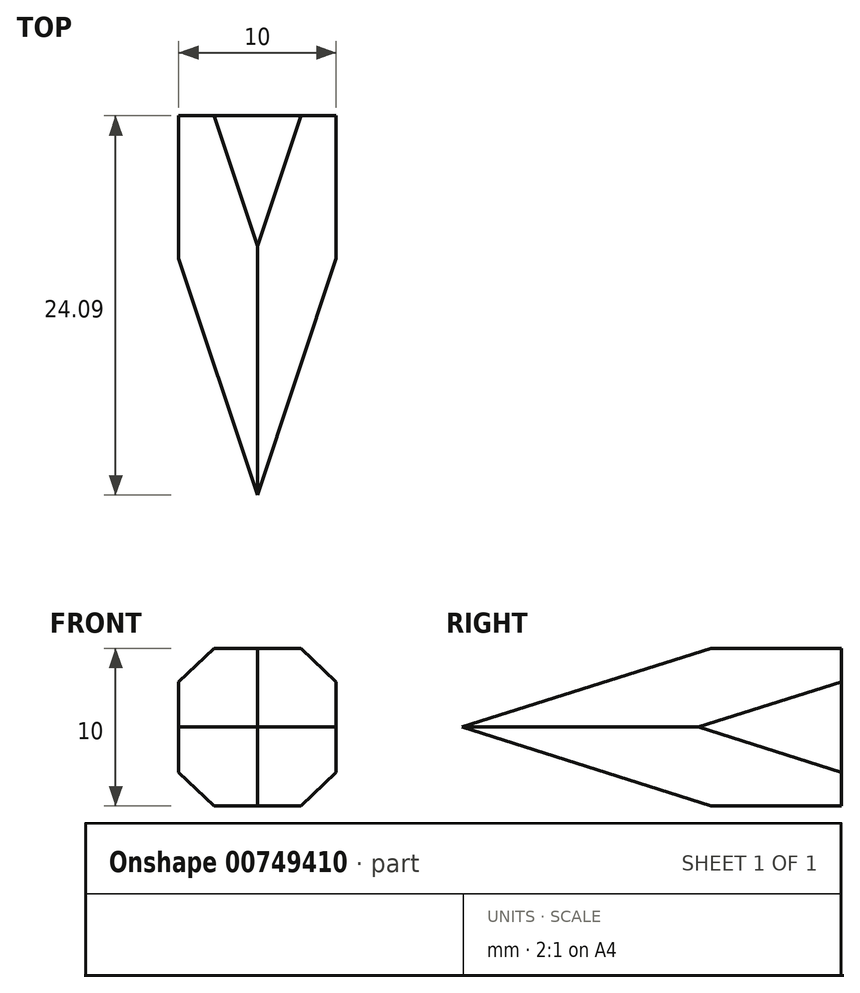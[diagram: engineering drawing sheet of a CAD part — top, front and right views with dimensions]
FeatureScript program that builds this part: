
annotation { "Feature Type Name" : "Feature", "Feature Type Description" : "" }
export const myFeature = defineFeature(function(context is Context, id is Id, definition is map)
    precondition{}
    {
        {
            var Q0;
            Q0=qCreatedBy(makeId("Top.planeOp"),FACE);
            var sketch = newSketch(context, id + "F0", { "sketchPlane" : qUnion([Q0])});
            skPoint(sketch, "E0.middle", {"position": v(0, 0) * mm});
            skLineSegment(sketch, "E1", {"start": v(0, -7.5) * mm, "end": v(-5, 7.5) * mm});
            skLineSegment(sketch, "E2", {"start": v(0, -7.5) * mm, "end": v(5, 7.5) * mm});
            skPoint(sketch, "E3.orphan", {"position": v(5, -7.5) * mm});
            skPoint(sketch, "E0.right.end.orphan", {"position": v(-5, -7.5) * mm});
            skLineSegment(sketch, "E4.bottom", {"start": v(-5, 16.59) * mm, "end": v(5, 16.59) * mm});
            skLineSegment(sketch, "E4.left", {"start": v(-5, 16.59) * mm, "end": v(-5, 7.5) * mm});
            skLineSegment(sketch, "E4.right", {"start": v(5, 16.59) * mm, "end": v(5, 7.5) * mm});
            skPoint(sketch, "E4.middle", {"position": v(0, 7.5) * mm});
            skPoint(sketch, "E5.orphan", {"position": v(-5, -1.59) * mm});
            skPoint(sketch, "E6.orphan", {"position": v(5, -1.59) * mm});
            skSolve(sketch);
        }
        {
            var Q0;
            Q0 = qSketchRegion(id + "F0", true);
            extrude(context, id + "F1", {"entities" : qUnion([Q0]), "endBound" : BoundingType.SYMMETRIC, "depth" : 10 * mm, "offsetDistance" : 25 * mm});
        }
        {
            var Q0;
            Q0=makeQuery(id+"F1.opExtrude","CAP_EDGE",EDGE,{"disambiguationData":[OSD([sQuery(id+"F0.wireOp",EDGE,"E2")])],"isStart":true});
            var Q1;
            Q1=makeQuery(id+"F1.opExtrude","CAP_EDGE",EDGE,{"disambiguationData":[OSD([sQuery(id+"F0.wireOp",EDGE,"E1")])],"isStart":true});
            var Q2;
            Q2=makeQuery(id+"F1.opExtrude","CAP_EDGE",EDGE,{"disambiguationData":[OSD([sQuery(id+"F0.wireOp",EDGE,"E2")])],"isStart":false});
            var Q3;
            Q3=makeQuery(id+"F1.opExtrude","CAP_EDGE",EDGE,{"disambiguationData":[OSD([sQuery(id+"F0.wireOp",EDGE,"E1")])],"isStart":false});
            chamfer(context, id + "F2", {"entities" : qUnion([Q0, Q1, Q2, Q3]), "width" : 5 * mm, "tangentPropagation" : true});
        }
    });
